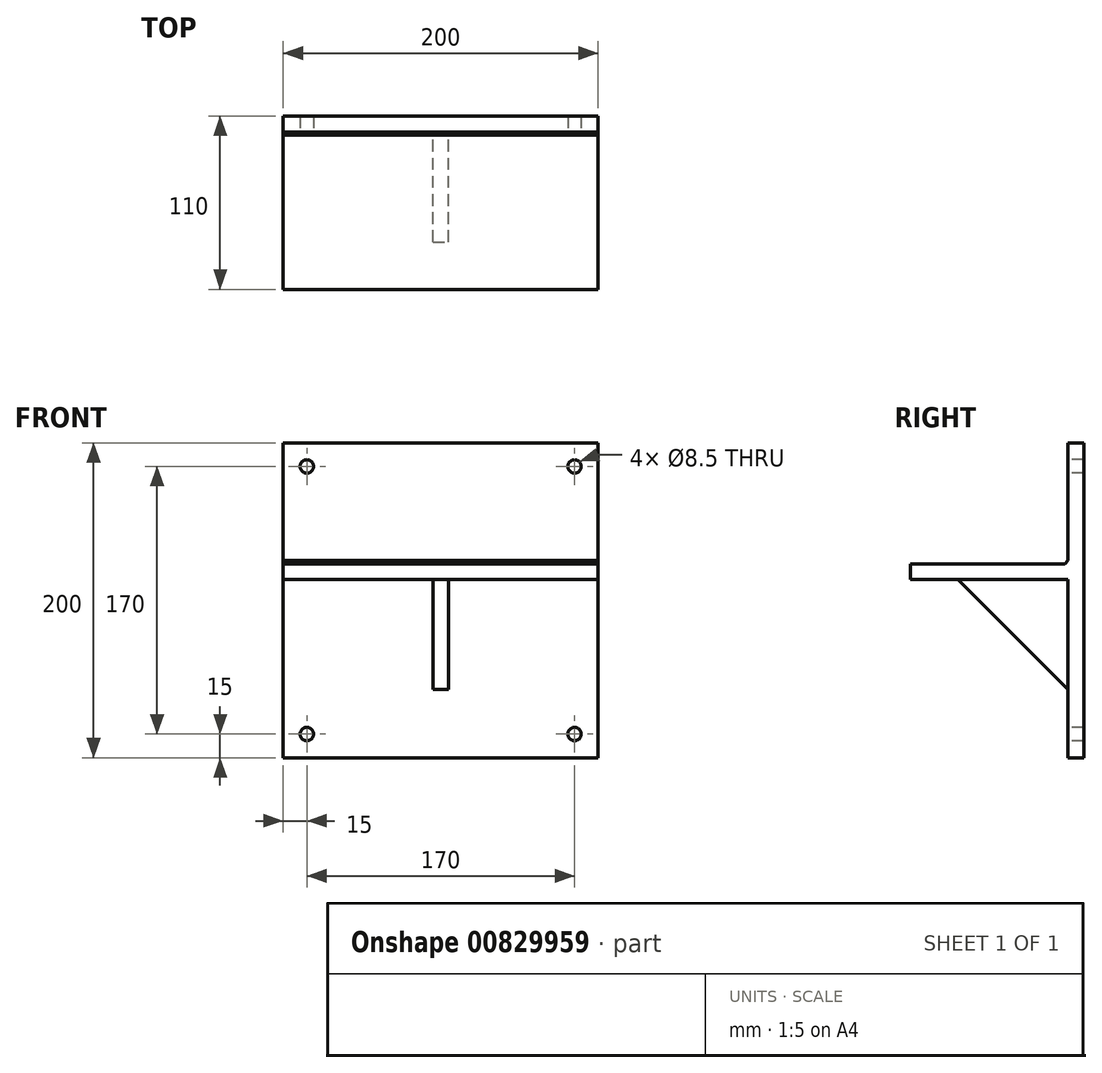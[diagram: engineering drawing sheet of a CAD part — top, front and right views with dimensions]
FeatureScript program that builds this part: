
annotation { "Feature Type Name" : "Feature", "Feature Type Description" : "" }
export const myFeature = defineFeature(function(context is Context, id is Id, definition is map)
    precondition{}
    {
        {
            var Q0;
            Q0=qCreatedBy(makeId("Front.planeOp"),FACE);
            var sketch = newSketch(context, id + "F0", { "sketchPlane" : qUnion([Q0])});
            skLineSegment(sketch, "E0.bottom", {"start": v(100, 100) * mm, "end": v(-100, 100) * mm});
            skLineSegment(sketch, "E0.top", {"start": v(100, -100) * mm, "end": v(-100, -100) * mm});
            skLineSegment(sketch, "E0.left", {"start": v(100, 100) * mm, "end": v(100, -100) * mm});
            skLineSegment(sketch, "E0.right", {"start": v(-100, 100) * mm, "end": v(-100, -100) * mm});
            skPoint(sketch, "E0.middle", {"position": v(0, 0) * mm});
            skSolve(sketch);
        }
        {
            var Q0;
            Q0=makeQuery(id+"F0.imprint","IMPRINT",FACE,{"disambiguationData":[TD([[makeQuery(id+"F0.imprint","IMPRINT",EDGE,{"derivedFrom":sQuery(id+"F0.wireOp",EDGE,"E0.bottom")}),1.0]])]});
            extrude(context, id + "F1", {"entities" : qUnion([Q0]), "depth" : 10 * mm, "offsetDistance" : 25 * mm});
        }
        {
            var Q0;
            Q0=makeQuery(id+"F1.opExtrude","CAP_FACE",FACE,{"disambiguationData":[OSD([sQuery(id+"F0.wireOp",EDGE,"E0.bottom"),sQuery(id+"F0.wireOp",EDGE,"E0.top"),sQuery(id+"F0.wireOp",EDGE,"E0.left"),sQuery(id+"F0.wireOp",EDGE,"E0.right")])],"isStart":false});
            var sketch = newSketch(context, id + "F2", { "sketchPlane" : qUnion([Q0])});
            skLineSegment(sketch, "E1", {"start": v(-100, 23.2) * mm, "end": v(100, 23.2) * mm});
            skLineSegment(sketch, "E2", {"start": v(-100, 13.2) * mm, "end": v(100, 13.2) * mm});
            skLineSegment(sketch, "E3", {"start": v(5, 13.2) * mm, "end": v(5, -56.8) * mm});
            skLineSegment(sketch, "E4.MirrorCS", {"start": v(-5, 13.2) * mm, "end": v(-5, -56.8) * mm});
            skLineSegment(sketch, "E5", {"start": v(-5, -56.8) * mm, "end": v(5, -56.8) * mm});
            skSolve(sketch);
        }
        {
            var Q0;
            {var subQ4=sQuery(id+"F2.wireOp",EDGE,"E1");Q0=makeQuery(id+"F2.imprint","IMPRINT",FACE,{"disambiguationData":[TD([[makeQuery(id+"F2.imprint","IMPRINT",EDGE,{"derivedFrom":subQ4}),-1.0]])]});}
            extrude(context, id + "F3", {"entities" : qUnion([Q0]), "operationType" : NewBodyOperationType.ADD, "depth" : 100 * mm, "offsetDistance" : 25 * mm});
        }
        {
            var Q0;
            {var subQ0=sQuery(id+"F2.wireOp",EDGE,"E3");Q0=makeQuery(id+"F2.imprint","IMPRINT",FACE,{"disambiguationData":[TD([[makeQuery(id+"F2.imprint","IMPRINT",EDGE,{"derivedFrom":subQ0}),-1.0]])]});}
            extrude(context, id + "F4", {"entities" : qUnion([Q0]), "operationType" : NewBodyOperationType.ADD, "depth" : 70 * mm, "offsetDistance" : 25 * mm});
        }
        {
            var Q0;
            Q0=makeQuery(id+"F4.opExtrude","SWEPT_FACE",FACE,{"disambiguationData":[OSD([sQuery(id+"F2.wireOp",EDGE,"E4.MirrorCS")])]});
            var sketch = newSketch(context, id + "F5", { "sketchPlane" : qUnion([Q0])});
            skLineSegment(sketch, "E6", {"start": v(10, -56.8) * mm, "end": v(80, 13.2) * mm});
            skSolve(sketch);
        }
        {
            var Q0;
            Q0=makeQuery(id+"F5.imprint","IMPRINT",FACE,{"disambiguationData":[TD([[makeQuery(id+"F5.imprint","IMPRINT",EDGE,{"derivedFrom":sQuery(id+"F5.wireOp",EDGE,"E6")}),-1.0]])]});
            extrude(context, id + "F6", {"entities" : qUnion([Q0]), "operationType" : NewBodyOperationType.REMOVE, "endBound" : BoundingType.THROUGH_ALL, "oppositeDirection" : true, "depth" : 25 * mm, "offsetDistance" : 25 * mm});
        }
        {
            var Q0;
            {var subQ0=sQuery(id+"F2.wireOp",EDGE,"E1");Q0=makeQuery(id+"F2.imprint","IMPRINT",FACE,{"disambiguationData":[TD([[makeQuery(id+"F2.imprint","IMPRINT",EDGE,{"derivedFrom":subQ0}),1.0]])]});}
            var sketch = newSketch(context, id + "F7", { "sketchPlane" : qUnion([Q0])});
            skPoint(sketch, "E7", {"position": v(-85, 85) * mm});
            skPoint(sketch, "E8.MirrorP", {"position": v(85, 85) * mm});
            skPoint(sketch, "E9.MirrorP", {"position": v(-85, -85) * mm});
            skPoint(sketch, "E10.MirrorP", {"position": v(85, -85) * mm});
            skSolve(sketch);
        }
        {
            var Q0;
            Q0=sQuery(id+"F7.wireOp",VERTEX,"E7");
            var Q1;
            Q1=sQuery(id+"F7.wireOp",VERTEX,"E8.MirrorP");
            var Q2;
            Q2=sQuery(id+"F7.wireOp",VERTEX,"E10.MirrorP");
            var Q3;
            Q3=sQuery(id+"F7.wireOp",VERTEX,"E9.MirrorP");
            var Q4;
            Q4=makeQuery(id+"F1.opExtrude","SWEPT_BODY",BODY,{"disambiguationData":[OSD([sQuery(id+"F0.wireOp",EDGE,"E0.bottom"),sQuery(id+"F0.wireOp",EDGE,"E0.top"),sQuery(id+"F0.wireOp",EDGE,"E0.left"),sQuery(id+"F0.wireOp",EDGE,"E0.right")])]});
            hole(context, id + "F8", {"style" : HoleStyle.SIMPLE, "endStyle" : HoleEndStyle.THROUGH, "holeDiameter" : 8.5 * mm, "majorDiameter" : 5 * mm, "isTappedThrough" : true, "tappedDepth" : 12 * mm, "tapClearance" : 3, "locations" : qUnion([Q0, Q1, Q2, Q3]), "scope" : qUnion([Q4])});
        }
        {
            var Q0;
            {var subQ0=sQuery(id+"F0.wireOp",EDGE,"E0.right");var subQ1=sQuery(id+"F2.wireOp",EDGE,"E2");Q0=makeQuery(id+"F4.boolean.opBoolean","SPLIT",EDGE,{"disambiguationData":[TD([makeQuery(id+"F1.opExtrude","SWEPT_FACE",FACE,{"disambiguationData":[OSD([subQ0])]})])],"derivedFrom":makeQuery(id+"F3.opExtrude","CAP_EDGE",EDGE,{"disambiguationData":[OSD([subQ1])],"isStart":true})});}
            var Q1;
            Q1=makeQuery(id+"F4.opExtrude","SWEPT_EDGE",EDGE,{"disambiguationData":[OSD([sQuery(id+"F2.wireOp",EDGE,"E2"),sQuery(id+"F2.wireOp",EDGE,"E4.MirrorCS")])]});
            var Q2;
            Q2=makeQuery(id+"F4.opExtrude","CAP_EDGE",EDGE,{"disambiguationData":[OSD([sQuery(id+"F2.wireOp",EDGE,"E4.MirrorCS")])],"isStart":true});
            var Q3;
            {var subQ0=sQuery(id+"F2.wireOp",EDGE,"E2");var subQ1=sQuery(id+"F0.wireOp",EDGE,"E0.left");Q3=makeQuery(id+"F4.boolean.opBoolean","SPLIT",EDGE,{"disambiguationData":[TD([makeQuery(id+"F1.opExtrude","SWEPT_FACE",FACE,{"disambiguationData":[OSD([subQ1])]})])],"derivedFrom":makeQuery(id+"F3.opExtrude","CAP_EDGE",EDGE,{"disambiguationData":[OSD([subQ0])],"isStart":true})});}
            var Q4;
            Q4=makeQuery(id+"F4.opExtrude","SWEPT_EDGE",EDGE,{"disambiguationData":[OSD([sQuery(id+"F2.wireOp",EDGE,"E2"),sQuery(id+"F2.wireOp",EDGE,"E3")])]});
            var Q5;
            Q5=makeQuery(id+"F4.opExtrude","CAP_EDGE",EDGE,{"disambiguationData":[OSD([sQuery(id+"F2.wireOp",EDGE,"E3")])],"isStart":true});
            var Q6;
            Q6=makeQuery(id+"F3.opExtrude","CAP_EDGE",EDGE,{"disambiguationData":[OSD([sQuery(id+"F2.wireOp",EDGE,"E1")])],"isStart":true});
            var Q7;
            {var subQ0=sQuery(id+"F2.wireOp",EDGE,"E5");Q7=makeQuery(id+"F6.boolean.opBoolean","MERGE",EDGE,{"derivedFrom":[makeQuery(id+"F4.opExtrude","CAP_EDGE",EDGE,{"disambiguationData":[OSD([subQ0])],"isStart":true}),makeQuery(id+"F6.opExtrude","SWEPT_EDGE",EDGE,{"disambiguationData":[OSD([sQuery(id+"F2.wireOp",EDGE,"E4.MirrorCS"),subQ0,sQuery(id+"F5.wireOp",EDGE,"E6")])]})]});}
            var Q8;
            {var subQ0=sQuery(id+"F2.wireOp",EDGE,"E2");Q8=makeQuery(id+"F6.boolean.opBoolean","MERGE",EDGE,{"derivedFrom":[makeQuery(id+"F4.opExtrude","CAP_EDGE",EDGE,{"disambiguationData":[OSD([subQ0])],"isStart":false}),makeQuery(id+"F6.opExtrude","SWEPT_EDGE",EDGE,{"disambiguationData":[OSD([subQ0,sQuery(id+"F2.wireOp",EDGE,"E4.MirrorCS"),sQuery(id+"F5.wireOp",EDGE,"E6")])]})]});}
            chamfer(context, id + "F9", {"entities" : qUnion([Q0, Q1, Q2, Q3, Q4, Q5, Q6, Q7, Q8]), "width" : 2 * mm, "tangentPropagation" : true});
        }
    });
